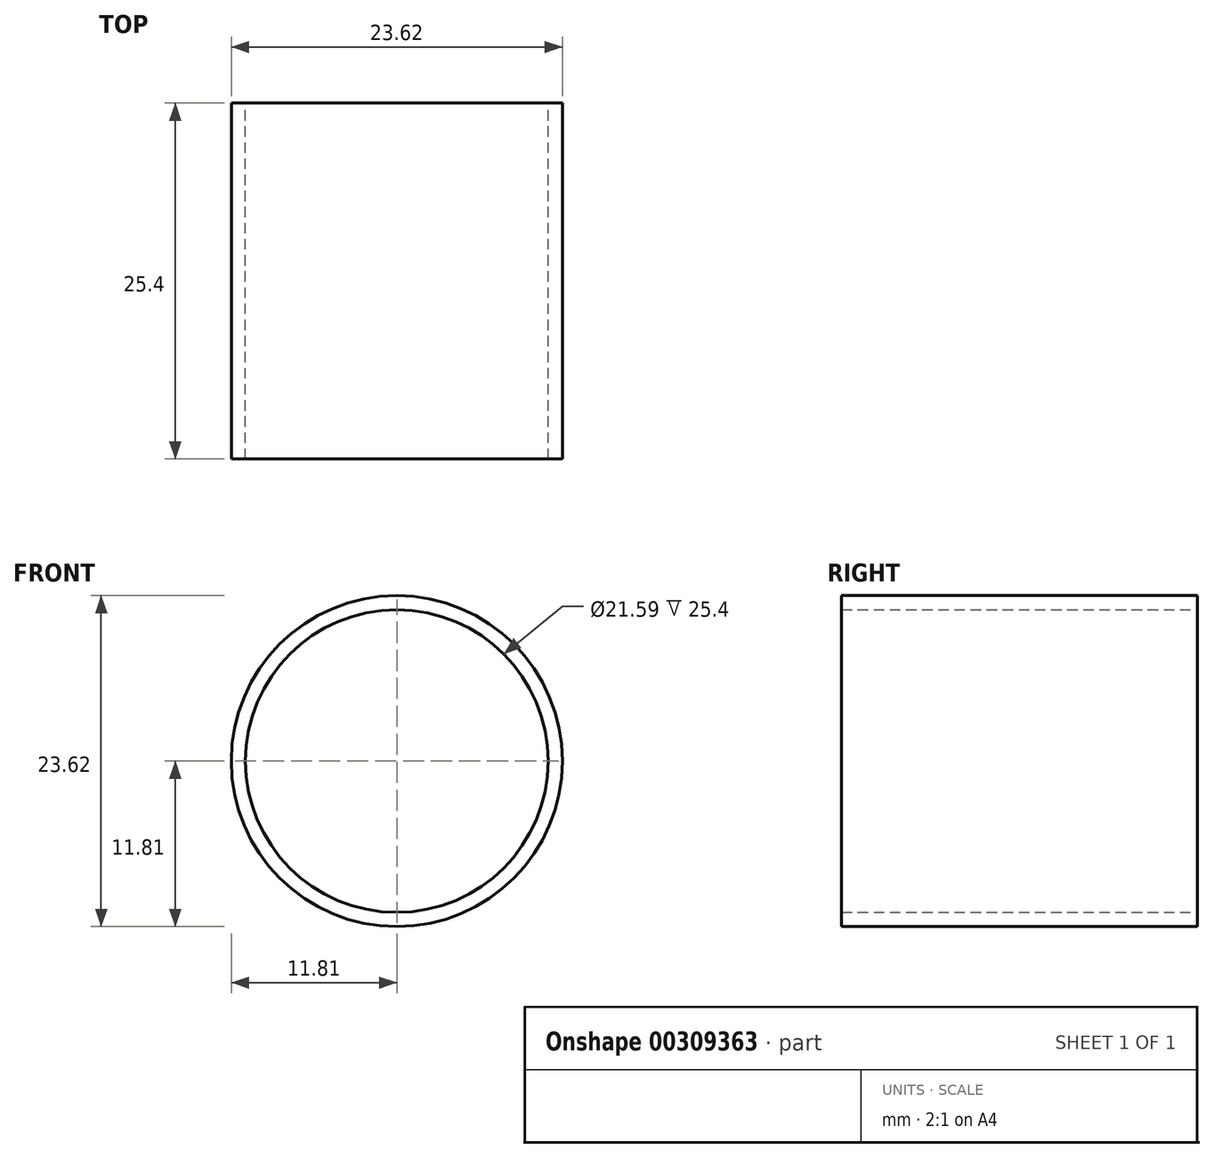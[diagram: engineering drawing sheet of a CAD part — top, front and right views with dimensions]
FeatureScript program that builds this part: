
annotation { "Feature Type Name" : "Feature", "Feature Type Description" : "" }
export const myFeature = defineFeature(function(context is Context, id is Id, definition is map)
    precondition{}
    {
        {
            var Q0;
            Q0=qCreatedBy(makeId("Front.planeOp"),FACE);
            var sketch = newSketch(context, id + "F0", { "sketchPlane" : qUnion([Q0])});
            skCircle(sketch, "E0", {"center": v(0, 0) * mm, "radius": 11.81 * mm});
            skCircle(sketch, "E1", {"center": v(0, 0) * mm, "radius": 10.8 * mm});
            skSolve(sketch);
        }
        {
            var Q0;
            Q0 = qSketchRegion(id + "F0", true);
            extrude(context, id + "F1", {"entities" : qUnion([Q0]), "depth" : 25.4 * mm});
        }
    });
